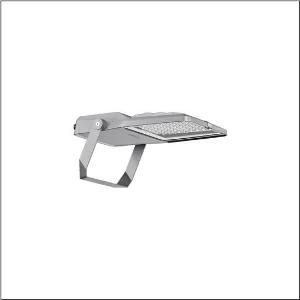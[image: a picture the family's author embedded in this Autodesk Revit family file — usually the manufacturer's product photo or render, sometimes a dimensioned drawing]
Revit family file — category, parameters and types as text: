
# Revit family: floodlight_fl_21_iq_mini___pl61_5xa7772d1c1a_27aa
name_source: partatom
category: Lighting Fixtures
units: mm (PartAtom-declared; Revit-internal decimal feet)

## family parameters
Cut with Voids When Loaded = No
Host = Face
Light Source = No
Part Type = Normal
Room Calculation Point = No
Round Connector Dimension = Use Diameter
Shared = No

## types (1)
- --- (1 x LED, 14490 lm, 143 W, 2200K)
    Apparent Load = 143 VA
    CIE Flux Codes = 33 65 98 100 100
    Color Rendering = 70
    Color Temperature = 2200K
    Default Elevation = 1800 mm
    Description = Floodlight FL 21 iQ mini, floodlight, primary light control with lens, of PMMA, primary optical cover: protective disc, of toughened safety glass, transparent, light distribution: PL61, light emission: direct distribution, installation type: surface-mounted, LED, High Power LED, rated luminous flux: 14.490lm, luminous efficacy: 101lm/W, light colour: 722, colour temperature: 2200K, control: Street-Remote, Auto-Match, Temp-Guard, Night-Set, Smart-Wire, Desk-Remote (wireless, voltage-free reading and setting of iQ features in the workshop via application-optimized NFC function/RFID function), optimised constant luminous flux control (CLO 2.0), with terminal, 6-pole, mains connection: 220..240V, AC, 50/60Hz, start of lifetime: 143W, end of service life: 152W, reduction: 61W, luminaire housing, of diecast aluminium, powder-coated, Siteco® metallic grey (DB 702S), corrosivity category C5 mid according to DIN EN ISO 12944, sealing non-destructively replaceable, mounting bracket, of steel, galvanised, powder-coated, Siteco® metallic grey (DB 702S), protection rating (complete): IP66, insulation class (complete): insulation class II (safety insulation), certification: CE, ENEC, VDE, protection symbol: D, impact resistance: IK08, permissible operating ambient temperature: -40..+40°C, permissible operating ambient temperature for outdoor applications: -40..+50°C, standard: DIN EN 12944, LABS conformity tested according to VDMA 24364:2018-05, packaging unit: 1 piece

Light Distribution: PL61
    Height = 70 mm
    Lamp = 1 x LED
    Lamp Light Flux = 14490 lm
    Lamp Power = 143 W
    Lamp count = 1
    Length = 485 mm
    Luminous efficacy = 101 lm/W
    Manufacturer = Siteco
    ModVariant = No
    Model = 5XA7772D1C1A
    Number of Poles = 1
    OnlyDefault = Yes
    Power Factor = 1
    Product Name = Floodlight FL 21 iQ mini | PL61
    Product group = floodlight | pylon annexe
    ProductGroupID = 6200
    Protection Class = Protection class II
    Protection Degree = IP 66
    RLX_Detail_Level = 1
    RLX_Emergency_Light_Flux = 0 lm
    RLX_Emergency_Type = 0
    RLX_Emergency_Type_DB = No
    RlxData = <blob elided: 96601 chars, md5=5f40e996>
    Socket = socket
    Standby Power = 0 W
    System Light Flux = 14490 lm
    System Power = 143 W
    Type Comments = factory setting: luminous flux: 100 % | dim-lin: 254 | 730 mA
    Type Image = l_1006845.jpg
    URL = http://relux.com
    VarID = @adj_105641
    Voltage = 0 V
    Weight = 0.00 kg
    Width = 337 mm

## geometry (parser evidence)
native form markers: Blend x4, Sweep x15
no freeform markers — native parametric forms only
